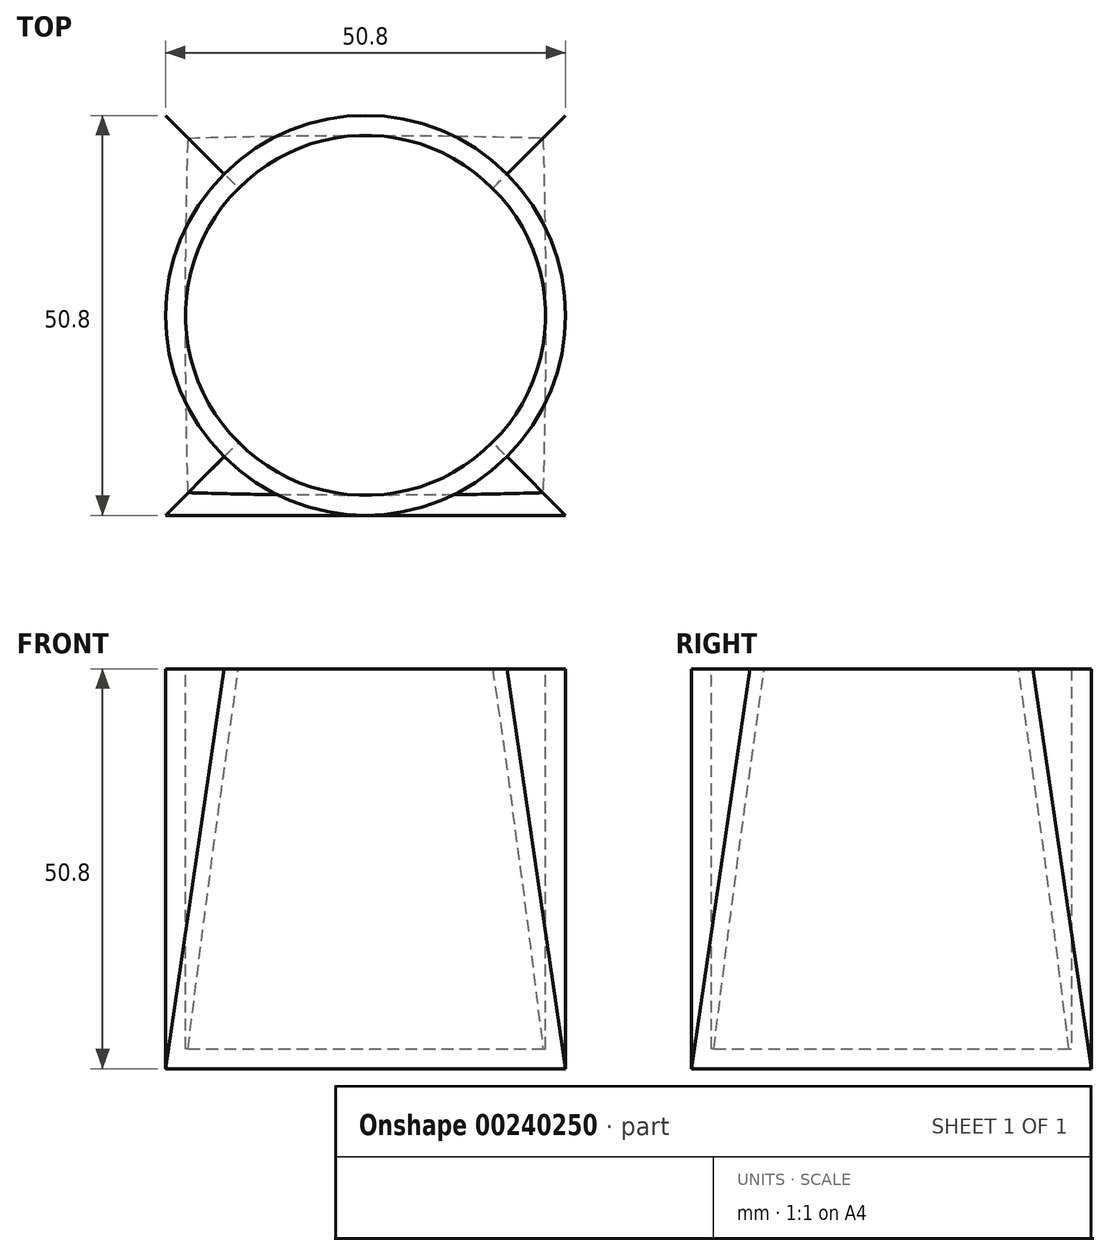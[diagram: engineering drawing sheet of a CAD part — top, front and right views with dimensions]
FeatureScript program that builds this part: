
annotation { "Feature Type Name" : "Feature", "Feature Type Description" : "" }
export const myFeature = defineFeature(function(context is Context, id is Id, definition is map)
    precondition{}
    {
        {
            var Q0;
            Q0=qCreatedBy(makeId("Top.planeOp"),FACE);
            cPlane(context, id + "F0", {"entities" : qUnion([Q0]), "cplaneType" : CPlaneType.OFFSET, "offset" : 50.8 * mm, "width" : 152.4 * mm, "height" : 152.4 * mm});
        }
        {
            var Q0;
            Q0=qCreatedBy(makeId("Top.planeOp"),FACE);
            var sketch = newSketch(context, id + "F1", { "sketchPlane" : qUnion([Q0])});
            skLineSegment(sketch, "E0.bottom", {"start": v(25.4, 25.4) * mm, "end": v(-25.4, 25.4) * mm});
            skLineSegment(sketch, "E0.top", {"start": v(25.4, -25.4) * mm, "end": v(-25.4, -25.4) * mm});
            skLineSegment(sketch, "E0.left", {"start": v(25.4, 25.4) * mm, "end": v(25.4, -25.4) * mm});
            skLineSegment(sketch, "E0.right", {"start": v(-25.4, 25.4) * mm, "end": v(-25.4, -25.4) * mm});
            skPoint(sketch, "E0.middle", {"position": v(0, 0) * mm});
            skSolve(sketch);
        }
        {
            var Q0;
            Q0=qCreatedBy(id+"F0.planeOp",FACE);
            var sketch = newSketch(context, id + "F2", { "sketchPlane" : qUnion([Q0])});
            skCircle(sketch, "E1", {"center": v(0, 0) * mm, "radius": 25.4 * mm});
            skSolve(sketch);
        }
        {
            var Q0;
            Q0=makeQuery(id+"F2.imprint","IMPRINT",FACE,{"disambiguationData":[TD([[makeQuery(id+"F2.imprint","IMPRINT",EDGE,{"derivedFrom":sQuery(id+"F2.wireOp",EDGE,"E1")}),1.0]])]});
            var Q1;
            Q1=makeQuery(id+"F1.imprint","IMPRINT",FACE,{"disambiguationData":[TD([[makeQuery(id+"F1.imprint","IMPRINT",EDGE,{"derivedFrom":sQuery(id+"F1.wireOp",EDGE,"E0.bottom")}),1.0]])]});
            loft(context, id + "F3", {"sheetProfilesArray" : [{ "sheetProfileEntities" : qUnion([Q0]) }, { "sheetProfileEntities" : qUnion([Q1]) }]});
        }
        {
            var Q0;
            Q0=makeQuery(id+"F3.opLoft","CAP_FACE",FACE,{"disambiguationData":[OSD([makeQuery(id+"F2.imprint","IMPRINT",FACE,{"disambiguationData":[TD([[makeQuery(id+"F2.imprint","IMPRINT",EDGE,{"derivedFrom":sQuery(id+"F2.wireOp",EDGE,"E1")}),1.0]])]})])],"isStart":true});
            shell(context, id + "F4", {"entities" : qUnion([Q0]), "thickness" : 2.54 * mm});
        }
    });
